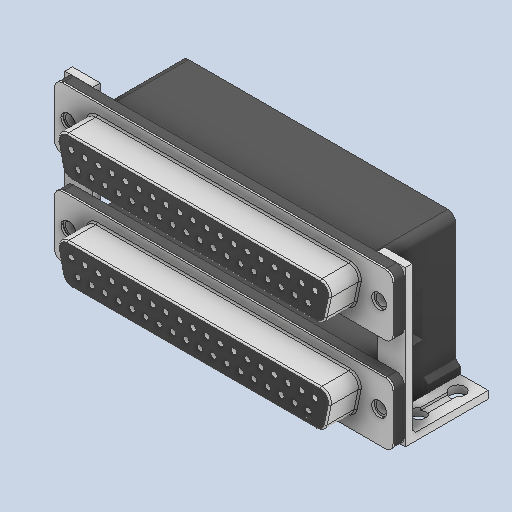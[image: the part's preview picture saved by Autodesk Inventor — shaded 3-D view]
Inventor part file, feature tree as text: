
AUTODESK INVENTOR PART (.ipt)
format: ipt  version: 2025 (Build 290162000, 162)  size: 1,036,800 bytes
history: native  units: in
note: dims shown in document units (in); Inventor stores cm internally (conversion verified against a paired STEP export)
features: extrude x1
ambient origin geometry x8: Origin, YZ Plane, XZ Plane, XY Plane, X Axis, Y Axis, Z Axis, Center Point
bodies: Solid1 (feature_tree)
feature tree (1):
  extrude  "Extrude32"  [1 undecoded]
note: 1 required parameter value undecoded (feature->parameter linkage not recoverable at this tier; creation-order binding heuristic only, values carry confidence <= 0.55)
